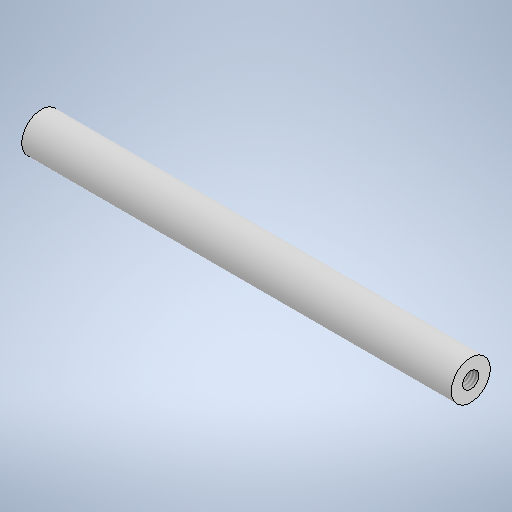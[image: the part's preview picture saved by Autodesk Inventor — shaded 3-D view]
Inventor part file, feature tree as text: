
AUTODESK INVENTOR PART (.ipt)
format: ipt  version: 2025 (Build 290162010, 162A)  size: 259,072 bytes
history: native  units: mm
features: sketch x3, hole x2, revolve x1
ambient origin geometry x8: Origin, YZ Plane, XZ Plane, XY Plane, X Axis, Y Axis, Z Axis, Center Point
bodies: Solid1 (feature_tree)
feature tree (6):
  revolve  "Revolution1"  [1 undecoded]
  hole  "Hole1"  [1 undecoded]
  hole  "Hole2"  [1 undecoded]
  sketch  "Sketch1"  dims[d0=110.0mm d1=10.0mm]
  sketch  "Sketch2"  dims[d2=90.0deg]
  sketch  "Sketch3"  dims[d3=4.134mm d4=10.0mm d5=4.0mm d6=2.0mm d7=90.0deg d8=14.2mm d9=0.0mm d10=4.134mm d11=12.0mm d12=4.0mm d13=2.0mm d14=90.0deg d15=12.0mm d16=0.0mm]
note: 3 required parameter values undecoded (feature->parameter linkage not recoverable at this tier; creation-order binding heuristic only, values carry confidence <= 0.55)